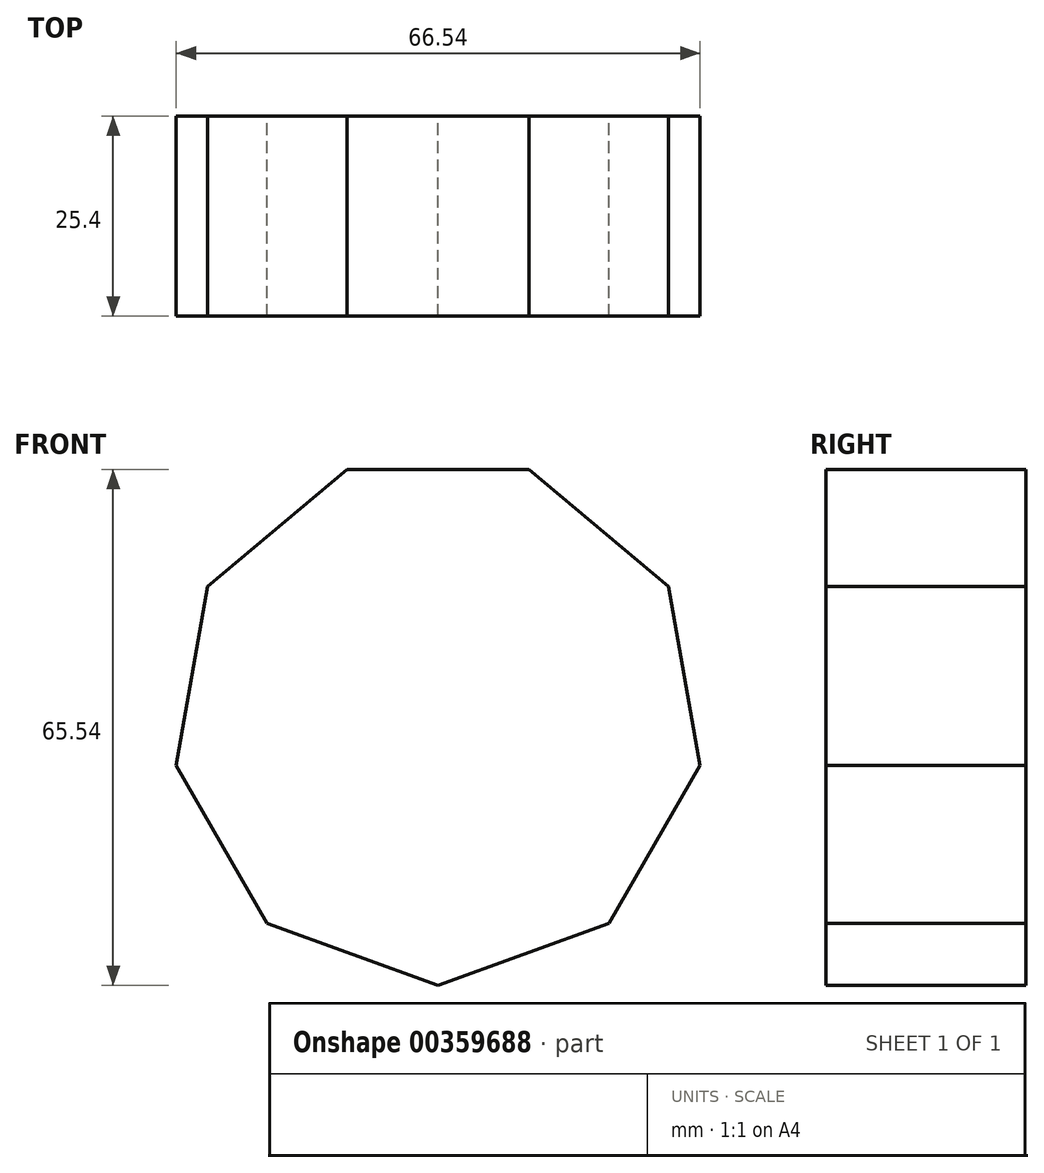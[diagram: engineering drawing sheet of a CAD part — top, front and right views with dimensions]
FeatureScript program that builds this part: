
annotation { "Feature Type Name" : "Feature", "Feature Type Description" : "" }
export const myFeature = defineFeature(function(context is Context, id is Id, definition is map)
    precondition{}
    {
        {
            var Q0;
            Q0=qCreatedBy(makeId("Front.planeOp"),FACE);
            var sketch = newSketch(context, id + "F0", { "sketchPlane" : qUnion([Q0])});
            skLineSegment(sketch, "E0", {"start": v(0, 0) * mm, "end": v(0, 31.75) * mm});
            skCircle(sketch, "E1.cCircle", {"center": v(0, 0) * mm, "radius": 31.75 * mm, "construction": true});
            skLineSegment(sketch, "E1.0", {"start": v(-11.56, 31.75) * mm, "end": v(11.56, 31.75) * mm});
            skLineSegment(sketch, "E1.1", {"start": v(11.56, 31.75) * mm, "end": v(29.26, 16.9) * mm});
            skLineSegment(sketch, "E1.2", {"start": v(29.26, 16.9) * mm, "end": v(33.27, -5.87) * mm});
            skLineSegment(sketch, "E1.3", {"start": v(33.27, -5.87) * mm, "end": v(21.72, -25.88) * mm});
            skLineSegment(sketch, "E1.4", {"start": v(21.72, -25.88) * mm, "end": v(0, -33.79) * mm});
            skLineSegment(sketch, "E1.5", {"start": v(0, -33.79) * mm, "end": v(-21.72, -25.88) * mm});
            skLineSegment(sketch, "E1.6", {"start": v(-21.72, -25.88) * mm, "end": v(-33.27, -5.87) * mm});
            skLineSegment(sketch, "E1.7", {"start": v(-33.27, -5.87) * mm, "end": v(-29.26, 16.9) * mm});
            skLineSegment(sketch, "E1.8", {"start": v(-29.26, 16.9) * mm, "end": v(-11.56, 31.75) * mm});
            skPoint(sketch, "E1.0.midPoint", {"position": v(0, 31.75) * mm});
            skSolve(sketch);
        }
        {
            var Q0;
            Q0 = qSketchRegion(id + "F0", true);
            var Q1;
            {var subQ0=sQuery(id+"F0.wireOp",EDGE,"E1.1");Q1=makeQuery(id+"F0.imprint","IMPRINT",FACE,{"disambiguationData":[TD([[makeQuery(id+"F0.imprint","IMPRINT",EDGE,{"derivedFrom":subQ0}),-1.0]])]});}
            extrude(context, id + "F1", {"entities" : qUnion([Q0, Q1]), "depth" : 25.4 * mm});
        }
    });
